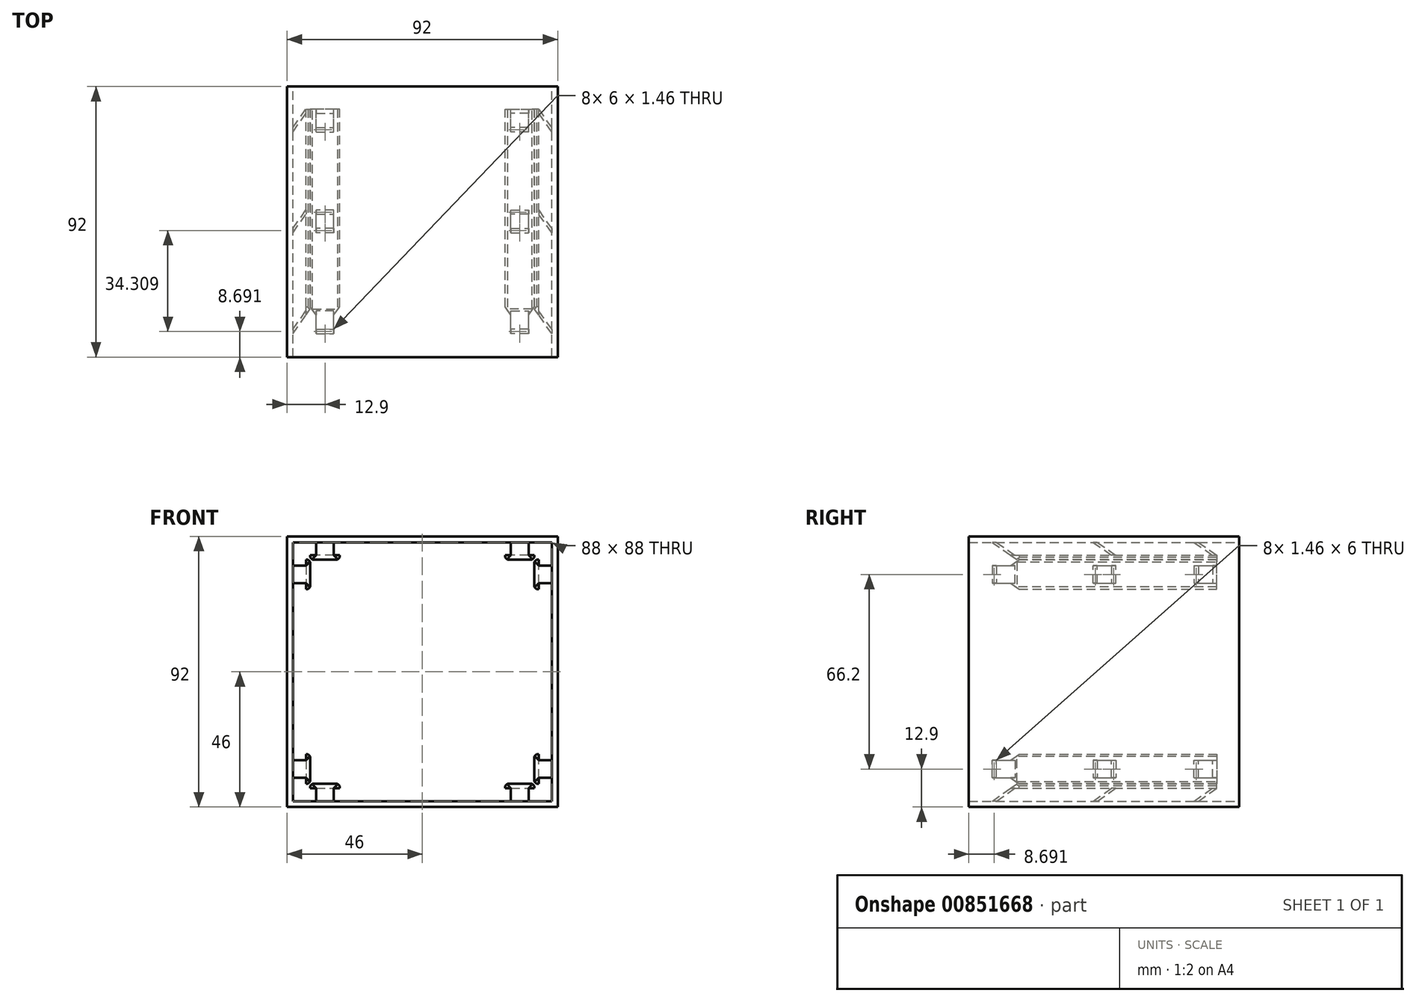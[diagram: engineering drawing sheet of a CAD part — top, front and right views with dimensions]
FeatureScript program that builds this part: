
annotation { "Feature Type Name" : "Feature", "Feature Type Description" : "" }
export const myFeature = defineFeature(function(context is Context, id is Id, definition is map)
    precondition{}
    {
        {
            var Q0;
            Q0=qCreatedBy(makeId("Front.planeOp"),FACE);
            var sketch = newSketch(context, id + "F0", { "sketchPlane" : qUnion([Q0])});
            skPoint(sketch, "E0.middle", {"position": v(0, 0) * mm});
            skLineSegment(sketch, "E1.bottom", {"start": v(38.1, -38.1) * mm, "end": v(-38.1, -38.1) * mm});
            skLineSegment(sketch, "E1.top", {"start": v(38.1, 38.1) * mm, "end": v(-38.1, 38.1) * mm});
            skLineSegment(sketch, "E1.left", {"start": v(38.1, -38.1) * mm, "end": v(38.1, 38.1) * mm});
            skLineSegment(sketch, "E1.right", {"start": v(-38.1, -38.1) * mm, "end": v(-38.1, 38.1) * mm});
            skLineSegment(sketch, "E2.bottom", {"start": v(-38.1, 39.6) * mm, "end": v(-28.1, 39.6) * mm});
            skLineSegment(sketch, "E2.top", {"start": v(-38.1, 38.1) * mm, "end": v(-28.1, 38.1) * mm});
            skLineSegment(sketch, "E2.left", {"start": v(-38.1, 39.6) * mm, "end": v(-38.1, 38.1) * mm});
            skLineSegment(sketch, "E2.right", {"start": v(-28.1, 39.6) * mm, "end": v(-28.1, 38.1) * mm});
            skLineSegment(sketch, "E3.MirrorCS", {"start": v(28.1, 39.6) * mm, "end": v(28.1, 38.1) * mm});
            skLineSegment(sketch, "E4.MirrorCS", {"start": v(38.1, 39.6) * mm, "end": v(28.1, 39.6) * mm});
            skLineSegment(sketch, "E5.MirrorCS", {"start": v(38.1, 39.6) * mm, "end": v(38.1, 38.1) * mm});
            skLineSegment(sketch, "E6.MirrorCS", {"start": v(38.1, 38.1) * mm, "end": v(28.1, 38.1) * mm});
            skLineSegment(sketch, "E7.1.1", {"start": v(-39.6, -38.1) * mm, "end": v(-39.6, -28.1) * mm});
            skLineSegment(sketch, "E7.1.2", {"start": v(-39.6, -28.1) * mm, "end": v(-38.1, -28.1) * mm});
            skLineSegment(sketch, "E7.1.3", {"start": v(-38.1, -38.1) * mm, "end": v(-38.1, -28.1) * mm});
            skLineSegment(sketch, "E7.1.4", {"start": v(-39.6, -38.1) * mm, "end": v(-38.1, -38.1) * mm});
            skLineSegment(sketch, "E7.2.1", {"start": v(38.1, -39.6) * mm, "end": v(28.1, -39.6) * mm});
            skLineSegment(sketch, "E7.2.2", {"start": v(28.1, -39.6) * mm, "end": v(28.1, -38.1) * mm});
            skLineSegment(sketch, "E7.2.3", {"start": v(38.1, -38.1) * mm, "end": v(28.1, -38.1) * mm});
            skLineSegment(sketch, "E7.2.4", {"start": v(38.1, -39.6) * mm, "end": v(38.1, -38.1) * mm});
            skLineSegment(sketch, "E7.3.1", {"start": v(39.6, 38.1) * mm, "end": v(39.6, 28.1) * mm});
            skLineSegment(sketch, "E7.3.2", {"start": v(39.6, 28.1) * mm, "end": v(38.1, 28.1) * mm});
            skLineSegment(sketch, "E7.3.3", {"start": v(38.1, 38.1) * mm, "end": v(38.1, 28.1) * mm});
            skLineSegment(sketch, "E7.3.4", {"start": v(39.6, 38.1) * mm, "end": v(38.1, 38.1) * mm});
            skLineSegment(sketch, "E8.1.1", {"start": v(-39.6, 28.1) * mm, "end": v(-38.1, 28.1) * mm});
            skLineSegment(sketch, "E8.1.2", {"start": v(-39.6, 38.1) * mm, "end": v(-39.6, 28.1) * mm});
            skLineSegment(sketch, "E8.1.3", {"start": v(-38.1, 38.1) * mm, "end": v(-38.1, 28.1) * mm});
            skLineSegment(sketch, "E8.1.4", {"start": v(-39.6, 38.1) * mm, "end": v(-38.1, 38.1) * mm});
            skLineSegment(sketch, "E8.2.1", {"start": v(-28.1, -39.6) * mm, "end": v(-28.1, -38.1) * mm});
            skLineSegment(sketch, "E8.2.2", {"start": v(-38.1, -39.6) * mm, "end": v(-28.1, -39.6) * mm});
            skLineSegment(sketch, "E8.2.3", {"start": v(-38.1, -38.1) * mm, "end": v(-28.1, -38.1) * mm});
            skLineSegment(sketch, "E8.2.4", {"start": v(-38.1, -39.6) * mm, "end": v(-38.1, -38.1) * mm});
            skLineSegment(sketch, "E8.3.1", {"start": v(39.6, -28.1) * mm, "end": v(38.1, -28.1) * mm});
            skLineSegment(sketch, "E8.3.2", {"start": v(39.6, -38.1) * mm, "end": v(39.6, -28.1) * mm});
            skLineSegment(sketch, "E8.3.3", {"start": v(38.1, -38.1) * mm, "end": v(38.1, -28.1) * mm});
            skLineSegment(sketch, "E8.3.4", {"start": v(39.6, -38.1) * mm, "end": v(38.1, -38.1) * mm});
            skLineSegment(sketch, "E9.bottom", {"start": v(46, -46) * mm, "end": v(-46, -46) * mm});
            skLineSegment(sketch, "E9.top", {"start": v(46, 46) * mm, "end": v(-46, 46) * mm});
            skLineSegment(sketch, "E9.left", {"start": v(46, -46) * mm, "end": v(46, 46) * mm});
            skLineSegment(sketch, "E9.right", {"start": v(-46, -46) * mm, "end": v(-46, 46) * mm});
            skLineSegment(sketch, "E10.bottom", {"start": v(44, -44) * mm, "end": v(-44, -44) * mm});
            skLineSegment(sketch, "E10.top", {"start": v(44, 44) * mm, "end": v(-44, 44) * mm});
            skLineSegment(sketch, "E10.left", {"start": v(44, -44) * mm, "end": v(44, 44) * mm});
            skLineSegment(sketch, "E10.right", {"start": v(-44, -44) * mm, "end": v(-44, 44) * mm});
            skLineSegment(sketch, "E11", {"start": v(0, -38.1) * mm, "end": v(0, 38.1) * mm});
            skLineSegment(sketch, "E12", {"start": v(-33.1, 39.6) * mm, "end": v(-33.1, 38.1) * mm});
            skSolve(sketch);
        }
        {
            var Q0;
            Q0=makeQuery(id+"F0.imprint","IMPRINT",FACE,{"disambiguationData":[TD([[makeQuery(id+"F0.imprint","IMPRINT",EDGE,{"derivedFrom":sQuery(id+"F0.wireOp",EDGE,"E9.bottom")}),-1.0]])]});
            extrude(context, id + "F1", {"entities" : qUnion([Q0]), "depth" : 92 * mm, "offsetDistance" : 25 * mm});
        }
        {
            var Q0;
            Q0=makeQuery(id+"F1.opExtrude","SWEPT_FACE",FACE,{"disambiguationData":[OSD([sQuery(id+"F0.wireOp",EDGE,"E10.top")])]});
            var sketch = newSketch(context, id + "F2", { "sketchPlane" : qUnion([Q0])});
            skLineSegment(sketch, "E13", {"start": v(-28.1, 0) * mm, "end": v(-28.1, 49) * mm});
            skLineSegment(sketch, "E14", {"start": v(-38.1, 0) * mm, "end": v(-38.1, 49) * mm});
            skLineSegment(sketch, "E15.bottom", {"start": v(-36.1, 15.42) * mm, "end": v(-30.1, 15.42) * mm});
            skLineSegment(sketch, "E15.top", {"start": v(-36.1, 13.96) * mm, "end": v(-30.1, 13.96) * mm});
            skLineSegment(sketch, "E15.left", {"start": v(-36.1, 15.42) * mm, "end": v(-36.1, 13.96) * mm});
            skLineSegment(sketch, "E15.right", {"start": v(-30.1, 15.42) * mm, "end": v(-30.1, 13.96) * mm});
            skLineSegment(sketch, "E16", {"start": v(-38.1, 49) * mm, "end": v(-28.1, 49) * mm});
            skLineSegment(sketch, "E17.MirrorCS", {"start": v(-36.1, 82.58) * mm, "end": v(-30.1, 82.58) * mm});
            skLineSegment(sketch, "E18.MirrorCS", {"start": v(-36.1, 82.58) * mm, "end": v(-36.1, 84.04) * mm});
            skLineSegment(sketch, "E19.MirrorCS", {"start": v(-36.1, 84.04) * mm, "end": v(-30.1, 84.04) * mm});
            skLineSegment(sketch, "E20.MirrorCS", {"start": v(-30.1, 82.58) * mm, "end": v(-30.1, 84.04) * mm});
            skLineSegment(sketch, "E21.bottom", {"start": v(-30.1, 48.27) * mm, "end": v(-36.1, 48.27) * mm});
            skLineSegment(sketch, "E21.top", {"start": v(-30.1, 49.73) * mm, "end": v(-36.1, 49.73) * mm});
            skLineSegment(sketch, "E21.left", {"start": v(-30.1, 48.27) * mm, "end": v(-30.1, 49.73) * mm});
            skLineSegment(sketch, "E21.right", {"start": v(-36.1, 48.27) * mm, "end": v(-36.1, 49.73) * mm});
            skPoint(sketch, "E21.middle", {"position": v(-33.1, 49) * mm});
            skSolve(sketch);
        }
        {
            var Q0;
            Q0=qCreatedBy(makeId("Top.planeOp"),FACE);
            var sketch = newSketch(context, id + "F3", { "sketchPlane" : qUnion([Q0])});
            skLineSegment(sketch, "E22", {"start": v(0, 0) * mm, "end": v(0, -92) * mm});
            skSolve(sketch);
        }
        {
            var Q0;
            Q0=sQuery(id+"F0.wireOp",EDGE,"E12");
            cPlane(context, id + "F4", {"entities" : qUnion([Q0]), "cplaneType" : CPlaneType.LINE_ANGLE, "offset" : 25 * mm, "angle" : 0 * degree, "width" : 150 * mm, "height" : 150 * mm});
        }
        {
            var Q0;
            Q0=qCreatedBy(id+"F4.planeOp",FACE);
            var sketch = newSketch(context, id + "F5", { "sketchPlane" : qUnion([Q0])});
            skLineSegment(sketch, "E23", {"start": v(84.04, 44) * mm, "end": v(75.61, 38.1) * mm});
            skLineSegment(sketch, "E24", {"start": v(75.61, 38.1) * mm, "end": v(0, 38.1) * mm});
            skLineSegment(sketch, "E25", {"start": v(77.75, 39.6) * mm, "end": v(0, 39.6) * mm});
            skLineSegment(sketch, "E26", {"start": v(0, 39.6) * mm, "end": v(0, 38.1) * mm});
            skSolve(sketch);
        }
        {
            var Q0;
            Q0=makeQuery(id+"F2.imprint","IMPRINT",FACE,{"disambiguationData":[TD([[makeQuery(id+"F2.imprint","IMPRINT",EDGE,{"derivedFrom":sQuery(id+"F2.wireOp",EDGE,"E17.MirrorCS")}),1.0]])]});
            var Q1;
            {var subQ5=sQuery(id+"F2.wireOp",EDGE,"E21.bottom");Q1=makeQuery(id+"F2.imprint","IMPRINT",FACE,{"disambiguationData":[TD([[makeQuery(id+"F2.imprint","IMPRINT",EDGE,{"derivedFrom":subQ5}),-1.0]])]});}
            var Q2;
            {var subQ5=sQuery(id+"F2.wireOp",EDGE,"E21.top");Q2=makeQuery(id+"F2.imprint","IMPRINT",FACE,{"disambiguationData":[TD([[makeQuery(id+"F2.imprint","IMPRINT",EDGE,{"derivedFrom":subQ5}),1.0]])]});}
            var Q3;
            Q3=makeQuery(id+"F2.imprint","IMPRINT",FACE,{"disambiguationData":[TD([[makeQuery(id+"F2.imprint","IMPRINT",EDGE,{"derivedFrom":sQuery(id+"F2.wireOp",EDGE,"E15.bottom")}),-1.0]])]});
            var Q4;
            Q4=sQuery(id+"F5.wireOp",EDGE,"E23");
            sweep(context, id + "F6", {"profiles" : qUnion([Q0, Q1, Q2, Q3]), "path" : qUnion([Q4])});
        }
        {
            var Q0;
            Q0 = qSketchRegion(id + "F5", true);
            extrude(context, id + "F7", {"entities" : qUnion([Q0]), "operationType" : NewBodyOperationType.ADD, "endBound" : BoundingType.SYMMETRIC, "depth" : 10 * mm, "offsetDistance" : 25 * mm});
        }
        {
            var Q0;
            {var subQ0=sQuery(id+"F5.wireOp",VERTEX,"E23.end");Q0=makeQuery(id+"F7.boolean.opBoolean","MERGE",FACE,{"derivedFrom":[makeQuery(id+"F6.opSweep","CAP_FACE",FACE,{"disambiguationData":[OSD([sQuery(id+"F2.wireOp",EDGE,"E15.bottom"),sQuery(id+"F2.wireOp",EDGE,"E15.top"),sQuery(id+"F2.wireOp",EDGE,"E15.left"),sQuery(id+"F2.wireOp",EDGE,"E15.right"),subQ0])],"isStart":false}),makeQuery(id+"F6.opSweep","CAP_FACE",FACE,{"disambiguationData":[OSD([sQuery(id+"F2.wireOp",EDGE,"E17.MirrorCS"),sQuery(id+"F2.wireOp",EDGE,"E18.MirrorCS"),sQuery(id+"F2.wireOp",EDGE,"E19.MirrorCS"),sQuery(id+"F2.wireOp",EDGE,"E20.MirrorCS"),subQ0])],"isStart":false}),makeQuery(id+"F6.opSweep","CAP_FACE",FACE,{"disambiguationData":[OSD([sQuery(id+"F2.wireOp",EDGE,"E21.bottom"),sQuery(id+"F2.wireOp",EDGE,"E21.top"),sQuery(id+"F2.wireOp",EDGE,"E21.left"),sQuery(id+"F2.wireOp",EDGE,"E21.right"),subQ0])],"isStart":false}),makeQuery(id+"F7.opExtrude","SWEPT_FACE",FACE,{"disambiguationData":[OSD([sQuery(id+"F5.wireOp",EDGE,"E24")])]})]});}
            var sketch = newSketch(context, id + "F8", { "sketchPlane" : qUnion([Q0])});
            skLineSegment(sketch, "E27", {"start": v(-36.1, 77.75) * mm, "end": v(-38.1, 74.9) * mm});
            skLineSegment(sketch, "E28", {"start": v(-38.1, 74.9) * mm, "end": v(-38.1, 77.75) * mm});
            skLineSegment(sketch, "E29", {"start": v(-38.1, 77.75) * mm, "end": v(-36.1, 77.75) * mm});
            skLineSegment(sketch, "E30.MirrorCS", {"start": v(-28.1, 74.9) * mm, "end": v(-28.1, 77.75) * mm});
            skLineSegment(sketch, "E31.MirrorCS", {"start": v(-28.1, 77.75) * mm, "end": v(-30.1, 77.75) * mm});
            skLineSegment(sketch, "E32.MirrorCS", {"start": v(-30.1, 77.75) * mm, "end": v(-28.1, 74.9) * mm});
            skLineSegment(sketch, "E33.bottom", {"start": v(-28.1, 0) * mm, "end": v(-38.1, 0) * mm});
            skLineSegment(sketch, "E33.top", {"start": v(-28.1, 7.68) * mm, "end": v(-38.1, 7.68) * mm});
            skLineSegment(sketch, "E33.left", {"start": v(-28.1, 0) * mm, "end": v(-28.1, 7.68) * mm});
            skLineSegment(sketch, "E33.right", {"start": v(-38.1, 0) * mm, "end": v(-38.1, 7.68) * mm});
            skSolve(sketch);
        }
        {
            var Q0;
            Q0 = qSketchRegion(id + "F8", true);
            extrude(context, id + "F9", {"entities" : qUnion([Q0]), "operationType" : NewBodyOperationType.REMOVE, "oppositeDirection" : true, "depth" : 3 * mm, "offsetDistance" : 25 * mm});
        }
        {
            var Q0;
            Q0=makeQuery(id+"F7.opExtrude","CAP_EDGE",EDGE,{"disambiguationData":[OSD([sQuery(id+"F5.wireOp",EDGE,"E24")])],"isStart":false});
            var Q1;
            Q1=makeQuery(id+"F7.opExtrude","CAP_EDGE",EDGE,{"disambiguationData":[OSD([sQuery(id+"F5.wireOp",EDGE,"E24")])],"isStart":true});
            chamfer(context, id + "F10", {"entities" : qUnion([Q0, Q1]), "width" : .75 * mm, "tangentPropagation" : true});
        }
        {
            var Q0;
            Q0=makeQuery(id+"F6.opSweep","SWEPT_BODY",BODY,{"disambiguationData":[OSD([sQuery(id+"F2.wireOp",EDGE,"E15.bottom"),sQuery(id+"F2.wireOp",EDGE,"E15.top"),sQuery(id+"F2.wireOp",EDGE,"E15.left"),sQuery(id+"F2.wireOp",EDGE,"E15.right"),sQuery(id+"F5.wireOp",EDGE,"E23")])]});
            var Q1;
            Q1=qCreatedBy(makeId("Right.planeOp"),FACE);
            mirror(context, id + "F11", {"entities" : qUnion([Q0]), "mirrorPlane" : qUnion([Q1])});
        }
        {
            var Q0;
            Q0=makeQuery(id+"F6.opSweep","SWEPT_BODY",BODY,{"disambiguationData":[OSD([sQuery(id+"F2.wireOp",EDGE,"E15.bottom"),sQuery(id+"F2.wireOp",EDGE,"E15.top"),sQuery(id+"F2.wireOp",EDGE,"E15.left"),sQuery(id+"F2.wireOp",EDGE,"E15.right"),sQuery(id+"F5.wireOp",EDGE,"E23")])]});
            var Q1;
            Q1=makeQuery(id+"F11.opPattern","COPY",BODY,{"derivedFrom":makeQuery(id+"F6.opSweep","SWEPT_BODY",BODY,{"disambiguationData":[OSD([sQuery(id+"F2.wireOp",EDGE,"E15.bottom"),sQuery(id+"F2.wireOp",EDGE,"E15.top"),sQuery(id+"F2.wireOp",EDGE,"E15.left"),sQuery(id+"F2.wireOp",EDGE,"E15.right"),sQuery(id+"F5.wireOp",EDGE,"E23")])]}),"instanceName":"1"});
            var Q2;
            Q2=sQuery(id+"F3.wireOp",EDGE,"E22");
            circularPattern(context, id + "F12", {"operationType" : NewBodyOperationType.ADD, "entities" : qUnion([Q0, Q1]), "axis" : qUnion([Q2]), "angle" : 360 * degree, "instanceCount" : 4, "equalSpace" : true});
        }
    });
